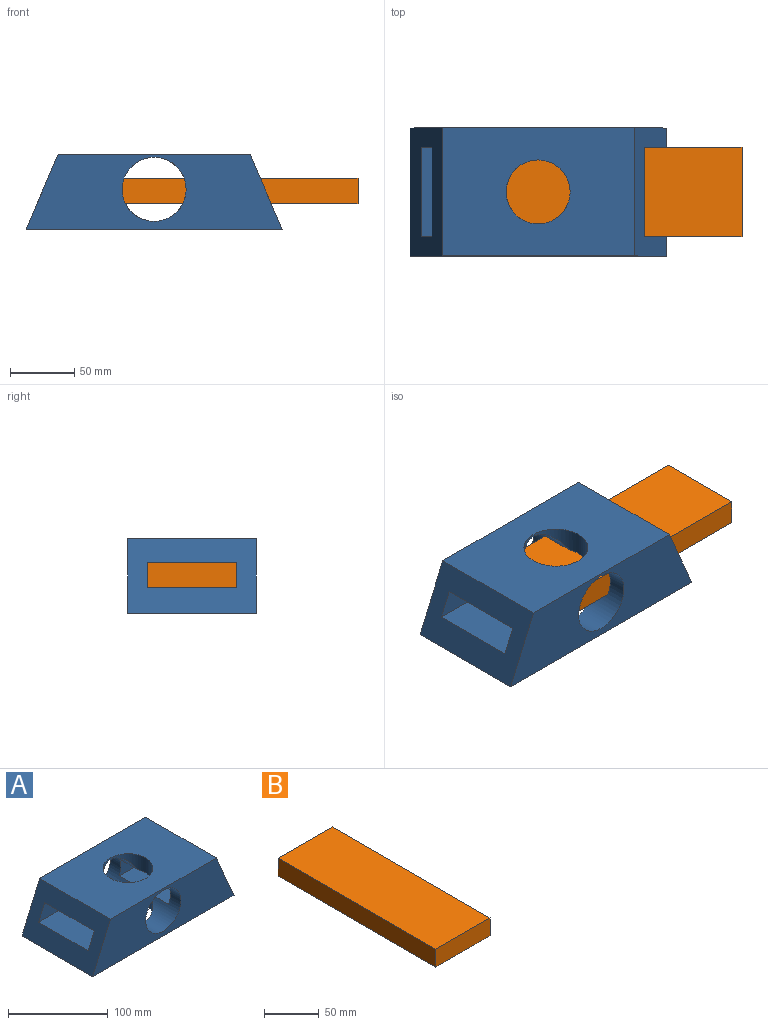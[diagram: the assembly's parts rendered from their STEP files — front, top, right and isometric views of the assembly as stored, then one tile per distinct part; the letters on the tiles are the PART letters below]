
ASSEMBLY  parts=2 mates=1
PART A: 18 faces, bbox 200x100x58.2 mm
  f0: plane 100x58.16mm, normal (-0.92,0,0.39), area 4806.3mm2, adj f4,f5,f6,f7,f14,f15,f16,f17
  f1: plane 100x58.16mm, normal (0.92,0,0.39), area 4806.3mm2, adj f4,f5,f6,f7,f10,f11,f12,f13
  f2: cylinder r=25mm len=50mm, axis (0,0,1), area 2140.6mm2, adj f4,f8,f9,f10,f17
  f3: cylinder r=25mm len=50mm, axis (0,0,1), area 1583mm2, adj f5,f8,f9,f11,f16
  f4: plane 200x100mm, normal (0,0,-1), area 18036.5mm2, adj f0,f1,f2,f6,f7
  f5: plane 150x100mm, normal (0,0,1), area 13036.5mm2, adj f0,f1,f3,f6,f7
  f6: plane 200x58.16mm, normal (0,-1,0), area 8213.8mm2, adj f0,f1,f4,f5,f8
  f7: plane 200x58.16mm, normal (0,1,0), area 8213.8mm2, adj f0,f1,f4,f5,f9
  f8: cylinder r=25mm len=50mm, axis (0,-1,0), area 4123.9mm2, adj f2,f3,f6,f10,f11,f13,f14,f16
  f9: cylinder r=25mm len=50mm, axis (0,-1,0), area 4123.9mm2, adj f2,f3,f7,f10,f11,f12,f15,f16
  f10: plane 70x69.03mm, normal (0,0,1), area 4792.6mm2, adj f1,f2,f8,f9,f12,f13
  f11: plane 70x59.42mm, normal (0,0,-1), area 4140.3mm2, adj f1,f3,f8,f9,f12,f13
  f12: plane 69.03x20mm, normal (0,-1,0), area 1256.3mm2, adj f1,f9,f10,f11
  f13: plane 69.03x20mm, normal (0,1,0), area 1256.3mm2, adj f1,f8,f10,f11
  f14: plane 69.03x20mm, normal (0,1,0), area 1256.3mm2, adj f0,f8,f16,f17
  f15: plane 69.03x20mm, normal (0,-1,0), area 1256.3mm2, adj f0,f9,f16,f17
  f16: plane 70x59.42mm, normal (0,0,-1), area 4140.3mm2, adj f0,f3,f8,f9,f14,f15
  f17: plane 70x69.03mm, normal (0,0,1), area 4792.6mm2, adj f0,f2,f8,f9,f14,f15
PART B: 6 faces, bbox 70x204x20 mm
  f0: plane 204x70mm, normal (0,0,1), area 14280mm2, adj f1,f3,f4,f5
  f1: plane 204x20mm, normal (-1,0,0), area 4080mm2, adj f0,f2,f4,f5
  f2: plane 204x70mm, normal (0,0,-1), area 14280mm2, adj f1,f3,f4,f5
  f3: plane 204x20mm, normal (1,0,0), area 4080mm2, adj f0,f2,f4,f5
  f4: plane 70x20mm, normal (0,-1,0), area 1400mm2, adj f0,f1,f2,f3
  f5: plane 70x20mm, normal (0,1,0), area 1400mm2, adj f0,f1,f2,f3
PLACE A t=(-77.89,-54.67,-48.65)mm fixed
PLACE B rot(axis=(-0.71,-0.71,0),180deg) t=(-20.72,-54.67,-13.63)mm
MATE fastened B.f0 <-> A.f10  axis (0,0,-1) through (-20.72,-54.67,-23.63)mm
